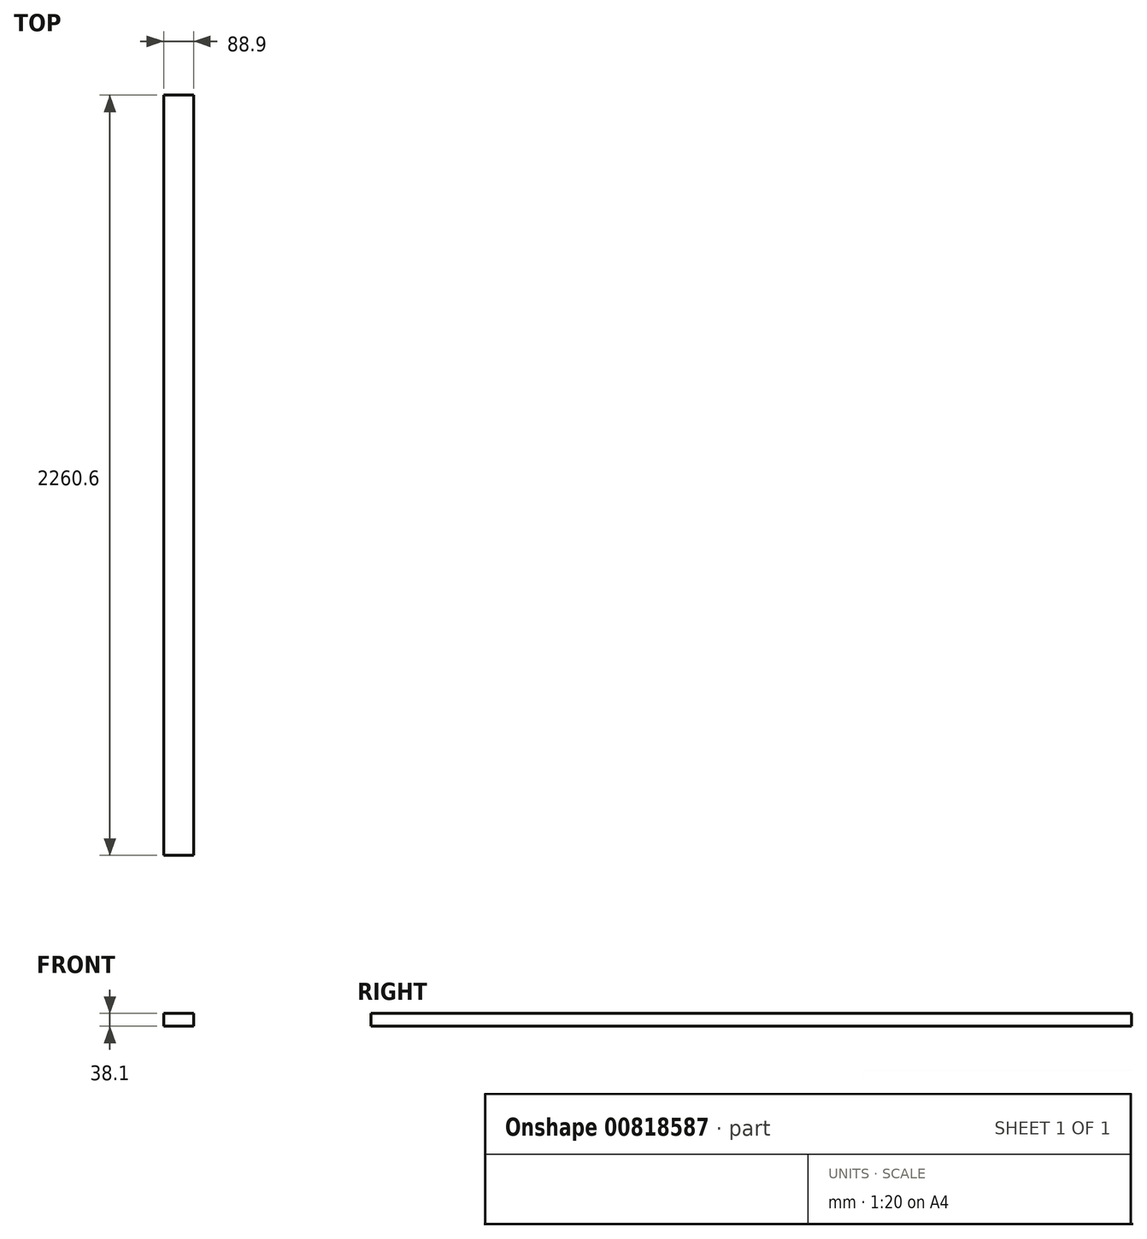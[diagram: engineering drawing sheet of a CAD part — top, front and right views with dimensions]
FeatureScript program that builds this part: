
annotation { "Feature Type Name" : "Feature", "Feature Type Description" : "" }
export const myFeature = defineFeature(function(context is Context, id is Id, definition is map)
    precondition{}
    {
        {
            var Q0;
            Q0=qCreatedBy(makeId("Front.planeOp"),FACE);
            var sketch = newSketch(context, id + "F0", { "sketchPlane" : qUnion([Q0])});
            skLineSegment(sketch, "E0.bottom", {"start": v(0, 0) * mm, "end": v(88.9, 0) * mm});
            skLineSegment(sketch, "E0.top", {"start": v(0, 38.1) * mm, "end": v(88.9, 38.1) * mm});
            skLineSegment(sketch, "E0.left", {"start": v(0, 0) * mm, "end": v(0, 38.1) * mm});
            skLineSegment(sketch, "E0.right", {"start": v(88.9, 0) * mm, "end": v(88.9, 38.1) * mm});
            skSolve(sketch);
        }
        {
            var Q0;
            Q0 = qSketchRegion(id + "F0", true);
            extrude(context, id + "F1", {"entities" : qUnion([Q0]), "oppositeDirection" : true, "depth" : 2260.6 * mm, "offsetDistance" : 25.4 * mm});
        }
    });
